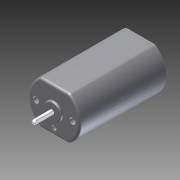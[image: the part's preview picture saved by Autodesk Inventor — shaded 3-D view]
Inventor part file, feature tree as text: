
AUTODESK INVENTOR PART (.ipt)
format: ipt  version: 2013 (Build 170138000, 138)  size: 171,008 bytes
history: native  units: in
note: dims shown in document units (in); Inventor stores cm internally (conversion verified against a paired STEP export)
features: extrude x6, sketch x5, fillet x3, chamfer x1, projected_geometry x1
ambient origin geometry x8: Origin, YZ Plane, XZ Plane, XY Plane, X Axis, Y Axis, Z Axis, Center Point
bodies: Solid1 (feature_tree)
feature tree (16):
  extrude  "Extrusion1"  Depth=0.787in TaperAngle=0.0deg
  fillet  "Fillet1"  Radius=0.02in
  sketch  "Sketch2"  dims[d4=0.02in d5=0.0in d6=0.01in d7=0.118in d8=0.0in]
  extrude  "Extrusion2"  Depth=0.01in
  fillet  "Fillet2"  Radius=0.118in
  extrude  "Extrusion3"  Depth=0.177in TaperAngle=0.0deg
  extrude  "Extrusion4"  Depth=0.197in
  fillet  "Fillet3"  Radius=0.047in
  extrude  "Extrusion5"  Depth=0.02in TaperAngle=45.0deg
  extrude  "Extrusion6"  [1 undecoded]
  chamfer  "Chamfer1"  [1 undecoded]
  sketch  "Sketch1"  dims[d0=0.039in d1=0.787in d2=0.0in d3=0.02in]
  sketch  "Sketch3"  dims[d9=0.039in d10=0.177in d11=0.0in]
  projected_geometry  "Projected Loop1"
  sketch  "Sketch4"  dims[d12=0.0195in d13=0.197in d14=0.047in d15=0.0in]
  sketch  "Sketch5"  dims[d16=0.063in d17=0.0in d18=0.02in d19=0.125in d20=45.0deg]
note: 2 required parameter values undecoded (feature->parameter linkage not recoverable at this tier; creation-order binding heuristic only, values carry confidence <= 0.55)
